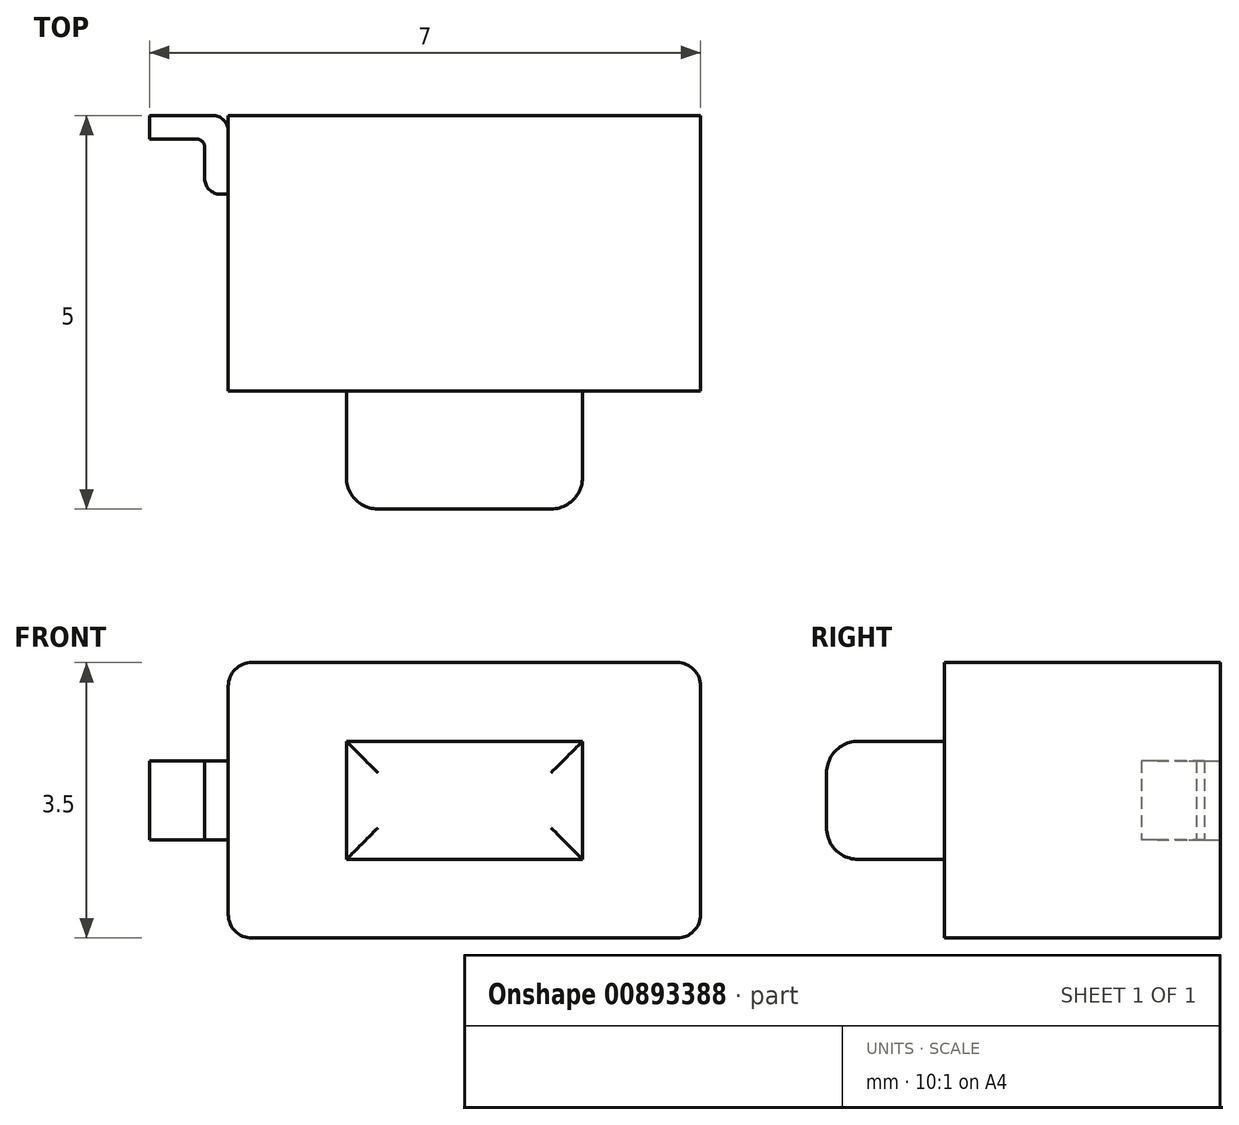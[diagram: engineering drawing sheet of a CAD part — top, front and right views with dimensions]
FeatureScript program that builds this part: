
annotation { "Feature Type Name" : "Feature", "Feature Type Description" : "" }
export const myFeature = defineFeature(function(context is Context, id is Id, definition is map)
    precondition{}
    {
        {
            var Q0;
            Q0=qCreatedBy(makeId("Front.planeOp"),FACE);
            var sketch = newSketch(context, id + "F0", { "sketchPlane" : qUnion([Q0])});
            skLineSegment(sketch, "E0.bottom", {"start": v(0, 0) * mm, "end": v(6, 0) * mm});
            skLineSegment(sketch, "E0.top", {"start": v(0, 3.5) * mm, "end": v(6, 3.5) * mm});
            skLineSegment(sketch, "E0.left", {"start": v(0, 0) * mm, "end": v(0, 3.5) * mm});
            skLineSegment(sketch, "E0.right", {"start": v(6, 0) * mm, "end": v(6, 3.5) * mm});
            skSolve(sketch);
        }
        {
            var Q0;
            Q0=makeQuery(id+"F0.imprint","IMPRINT",FACE,{"disambiguationData":[TD([[makeQuery(id+"F0.imprint","IMPRINT",EDGE,{"derivedFrom":sQuery(id+"F0.wireOp",EDGE,"E0.bottom")}),1.0]])]});
            extrude(context, id + "F1", {"entities" : qUnion([Q0]), "depth" : 3.5 * mm, "offsetDistance" : 25 * mm});
        }
        {
            var Q0;
            Q0=makeQuery(id+"F1.opExtrude","CAP_FACE",FACE,{"disambiguationData":[OSD([sQuery(id+"F0.wireOp",EDGE,"E0.bottom"),sQuery(id+"F0.wireOp",EDGE,"E0.top"),sQuery(id+"F0.wireOp",EDGE,"E0.left"),sQuery(id+"F0.wireOp",EDGE,"E0.right")])],"isStart":false});
            var sketch = newSketch(context, id + "F2", { "sketchPlane" : qUnion([Q0])});
            skLineSegment(sketch, "E1.0.0", {"start": v(0, 3.5) * mm, "end": v(0, 0) * mm});
            skLineSegment(sketch, "E1.0.1", {"start": v(0, 0) * mm, "end": v(6, 0) * mm});
            skLineSegment(sketch, "E1.0.2", {"start": v(6, 0) * mm, "end": v(6, 3.5) * mm});
            skLineSegment(sketch, "E1.0.3", {"start": v(6, 3.5) * mm, "end": v(0, 3.5) * mm});
            skLineSegment(sketch, "E2.bottom", {"start": v(1.5, 2.5) * mm, "end": v(4.5, 2.5) * mm});
            skLineSegment(sketch, "E2.top", {"start": v(1.5, 1) * mm, "end": v(4.5, 1) * mm});
            skLineSegment(sketch, "E2.left", {"start": v(1.5, 2.5) * mm, "end": v(1.5, 1) * mm});
            skLineSegment(sketch, "E2.right", {"start": v(4.5, 2.5) * mm, "end": v(4.5, 1) * mm});
            skPoint(sketch, "E2.middle", {"position": v(3, 1.75) * mm});
            skPoint(sketch, "E2.middle.positionSnap0", {"position": v(0, 1.75) * mm});
            skPoint(sketch, "E2.middle.positionSnap1", {"position": v(3, 3.5) * mm});
            skPoint(sketch, "E2.centerSnap0", {"position": v(0, 1.75) * mm});
            skPoint(sketch, "E2.centerSnap1", {"position": v(3, 3.5) * mm});
            skSolve(sketch);
        }
        {
            var Q0;
            Q0=makeQuery(id+"F2.imprint","IMPRINT",FACE,{"disambiguationData":[TD([[makeQuery(id+"F2.imprint","IMPRINT",EDGE,{"derivedFrom":sQuery(id+"F2.wireOp",EDGE,"E2.bottom")}),-1.0]])]});
            extrude(context, id + "F3", {"entities" : qUnion([Q0]), "operationType" : NewBodyOperationType.ADD, "depth" : 1.5 * mm, "offsetDistance" : 25 * mm});
        }
        {
            var Q0;
            Q0=makeQuery(id+"F1.opExtrude","SWEPT_EDGE",EDGE,{"disambiguationData":[OSD([sQuery(id+"F0.wireOp",EDGE,"E0.bottom"),sQuery(id+"F0.wireOp",EDGE,"E0.left")])]});
            var Q1;
            Q1=makeQuery(id+"F1.opExtrude","SWEPT_EDGE",EDGE,{"disambiguationData":[OSD([sQuery(id+"F0.wireOp",EDGE,"E0.top"),sQuery(id+"F0.wireOp",EDGE,"E0.left")])]});
            var Q2;
            Q2=makeQuery(id+"F1.opExtrude","SWEPT_EDGE",EDGE,{"disambiguationData":[OSD([sQuery(id+"F0.wireOp",EDGE,"E0.bottom"),sQuery(id+"F0.wireOp",EDGE,"E0.right")])]});
            var Q3;
            Q3=makeQuery(id+"F1.opExtrude","SWEPT_EDGE",EDGE,{"disambiguationData":[OSD([sQuery(id+"F0.wireOp",EDGE,"E0.top"),sQuery(id+"F0.wireOp",EDGE,"E0.right")])]});
            fillet(context, id + "F4", {"entities" : qUnion([Q0, Q1, Q2, Q3]), "tangentPropagation" : true, "radius" : 0.3 * mm, "defaultsChanged" : true, "vertexSettings" : [], "allowEdgeOverflow" : false});
        }
        {
            var Q0;
            Q0=makeQuery(id+"F3.opExtrude","CAP_EDGE",EDGE,{"disambiguationData":[OSD([sQuery(id+"F2.wireOp",EDGE,"E2.left")])],"isStart":false});
            var Q1;
            Q1=makeQuery(id+"F3.opExtrude","CAP_EDGE",EDGE,{"disambiguationData":[OSD([sQuery(id+"F2.wireOp",EDGE,"E2.bottom")])],"isStart":false});
            var Q2;
            Q2=makeQuery(id+"F3.opExtrude","CAP_EDGE",EDGE,{"disambiguationData":[OSD([sQuery(id+"F2.wireOp",EDGE,"E2.top")])],"isStart":false});
            var Q3;
            Q3=makeQuery(id+"F3.opExtrude","CAP_EDGE",EDGE,{"disambiguationData":[OSD([sQuery(id+"F2.wireOp",EDGE,"E2.right")])],"isStart":false});
            fillet(context, id + "F5", {"entities" : qUnion([Q0, Q1, Q2, Q3]), "tangentPropagation" : true, "radius" : 0.4 * mm, "defaultsChanged" : true, "vertexSettings" : [], "allowEdgeOverflow" : false});
        }
        {
            var Q0;
            Q0=makeQuery(id+"F1.opExtrude","SWEPT_FACE",FACE,{"disambiguationData":[OSD([sQuery(id+"F0.wireOp",EDGE,"E0.top")])]});
            var Q1;
            Q1=makeQuery(id+"F1.opExtrude","SWEPT_FACE",FACE,{"disambiguationData":[OSD([sQuery(id+"F0.wireOp",EDGE,"E0.bottom")])]});
            cPlane(context, id + "F6", {"entities" : qUnion([Q0, Q1]), "cplaneType" : CPlaneType.MID_PLANE, "offset" : 25 * mm, "width" : 150 * mm, "height" : 150 * mm});
        }
        {
            var Q0;
            Q0=qCreatedBy(id+"F6.planeOp",FACE);
            var sketch = newSketch(context, id + "F7", { "sketchPlane" : qUnion([Q0])});
            skLineSegment(sketch, "E3", {"start": v(0, -1) * mm, "end": v(-0.1, -1) * mm});
            skLineSegment(sketch, "E4", {"start": v(-0.3, -0.8) * mm, "end": v(-0.3, -0.4) * mm});
            skLineSegment(sketch, "E5", {"start": v(-0.4, -0.3) * mm, "end": v(-1, -0.3) * mm});
            skLineSegment(sketch, "E6", {"start": v(-1, -0.3) * mm, "end": v(-1, 0) * mm});
            skLineSegment(sketch, "E7", {"start": v(-1, 0) * mm, "end": v(-0.2, 0) * mm});
            skLineSegment(sketch, "E8", {"start": v(0, -0.2) * mm, "end": v(0, -1) * mm});
            skPoint(sketch, "E9.visualSharp", {"position": v(0, 0) * mm});
            skArc(sketch, "E9.filletArc", {"start": v(0, -0.2) * mm, "mid": v(-0.06, -0.06) * mm, "end": v(-0.2, 0) * mm});
            skPoint(sketch, "E10.visualSharp", {"position": v(-0.3, -0.3) * mm});
            skArc(sketch, "E10.filletArc", {"start": v(-0.3, -0.4) * mm, "mid": v(-0.33, -0.33) * mm, "end": v(-0.4, -0.3) * mm});
            skPoint(sketch, "E11.visualSharp", {"position": v(-0.3, -1) * mm});
            skArc(sketch, "E11.filletArc", {"start": v(-0.3, -0.8) * mm, "mid": v(-0.24, -0.94) * mm, "end": v(-0.1, -1) * mm});
            skSolve(sketch);
        }
        {
            var Q0;
            Q0=makeQuery(id+"F7.imprint","IMPRINT",FACE,{"disambiguationData":[TD([[makeQuery(id+"F7.imprint","IMPRINT",EDGE,{"derivedFrom":sQuery(id+"F7.wireOp",EDGE,"E3")}),-1.0]])]});
            extrude(context, id + "F8", {"entities" : qUnion([Q0]), "operationType" : NewBodyOperationType.ADD, "endBound" : BoundingType.SYMMETRIC, "depth" : 1 * mm, "offsetDistance" : 25 * mm});
        }
        {
            var Q0;
            Q0=makeQuery(id+"F1.opExtrude","SWEPT_FACE",FACE,{"disambiguationData":[OSD([sQuery(id+"F0.wireOp",EDGE,"E0.left")])]});
            var Q1;
            Q1=makeQuery(id+"F1.opExtrude","SWEPT_FACE",FACE,{"disambiguationData":[OSD([sQuery(id+"F0.wireOp",EDGE,"E0.right")])]});
            cPlane(context, id + "F9", {"entities" : qUnion([Q0, Q1]), "cplaneType" : CPlaneType.MID_PLANE, "offset" : 25 * mm, "width" : 150 * mm, "height" : 150 * mm});
        }
    });
